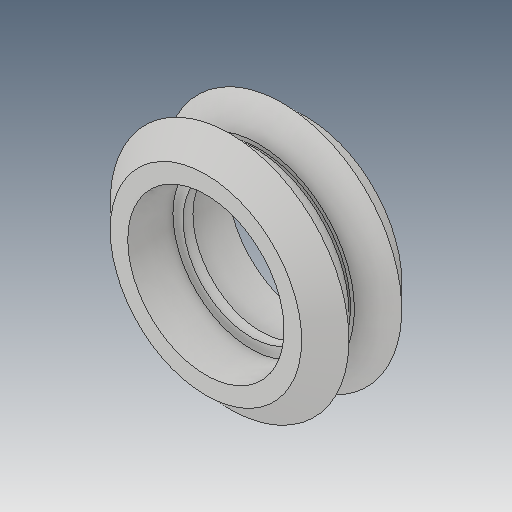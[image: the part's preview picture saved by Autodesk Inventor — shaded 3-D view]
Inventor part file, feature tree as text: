
AUTODESK INVENTOR PART (.ipt)
format: ipt  version: 2017 (Build 210142000, 142)  size: 157,184 bytes
history: native  units: mm
features: sketch x5, other x3
ambient origin geometry x8: Origin, YZ Plane, XZ Plane, XY Plane, X Axis, Y Axis, Z Axis, Center Point
bodies: Solid1 (feature_tree)
feature tree (8):
  other  "dELRIN.ipt"
  other  "Solid1::dELRIN.ipt"
  other  "TaggingFeature1"
  sketch  "Sketch1"  dims[d0=10.0mm]
  sketch  "Sketch2"
  sketch  "Sketch3"
  sketch  "Sketch4"
  sketch  "Sketch5"
